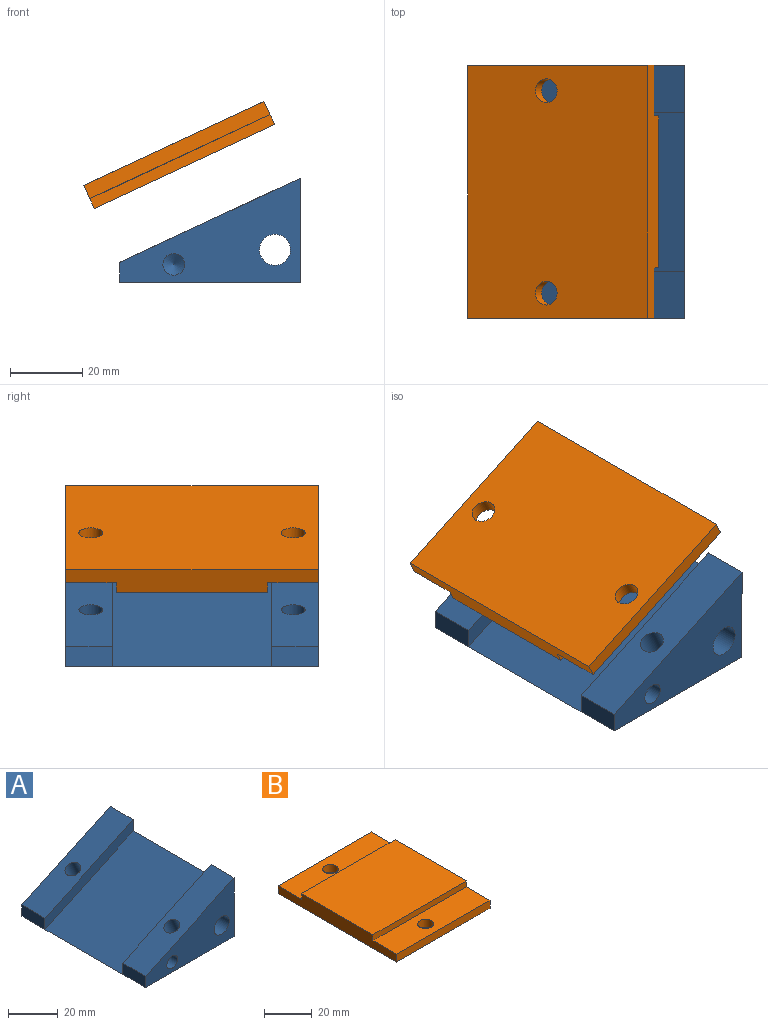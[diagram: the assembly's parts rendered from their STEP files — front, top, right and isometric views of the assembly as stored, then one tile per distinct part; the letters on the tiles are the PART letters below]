
ASSEMBLY  parts=2 mates=1
PART A: 32 faces, bbox 50x70x28.8 mm
  f0: cylinder r=3.3mm len=11.85mm, axis (-0.42,0,0.91), area 207.4mm2, adj f11,f26
  f1: cylinder r=3.3mm len=11.85mm, axis (-0.42,0,0.91), area 207.4mm2, adj f2,f19
  f2: plane 50x23.32mm, normal (-0.42,0,0.91), area 682.9mm2, adj f1,f5,f6,f8,f9
  f3: plane 50x44mm, normal (-0.42,0,0.91), area 2427.4mm2, adj f4,f5,f9,f12
  f4: plane 70x50mm, normal (0,0,-1), area 3285.3mm2, adj f3,f5,f6,f7,f8,f10,f13,f14
  f5: plane 70x28.83mm, normal (1,0,0), area 1775.5mm2, adj f2,f3,f4,f6,f7,f9,f11,f12
  f6: plane 50x28.83mm, normal (0,-1,0), area 772.4mm2, adj f2,f4,f5,f8,f27,f28
  f7: plane 50x28.83mm, normal (0,1,0), area 772.4mm2, adj f4,f5,f10,f11,f27,f30
  f8: plane 13x5.52mm, normal (-1,0,0), area 71.7mm2, adj f2,f4,f6,f9
  f9: plane 50x28.83mm, normal (0,1,0), area 275.8mm2, adj f2,f3,f5,f8
  f10: plane 13x5.52mm, normal (-1,0,0), area 71.7mm2, adj f4,f7,f11,f12
  f11: plane 50x23.31mm, normal (-0.42,0,0.91), area 683mm2, adj f0,f5,f7,f10,f12
  f12: plane 50x28.83mm, normal (0,-1,0), area 275.9mm2, adj f3,f5,f10,f11
  f13: plane 9.23x7.89mm, normal (0,-1,0), area 44.5mm2, adj f4,f14,f18,f19
  f14: plane 9.18x7.06mm, normal (-0.78,-0.5,-0.37), area 57.6mm2, adj f4,f13,f15,f19
  f15: plane 9.18x7.06mm, normal (-0.78,0.5,-0.37), area 57.6mm2, adj f4,f14,f16,f19
  f16: plane 9.23x7.89mm, normal (0,1,0), area 44.5mm2, adj f4,f15,f17,f19
  f17: plane 5.3x5.3mm, normal (0.78,0.5,0.37), area 31.4mm2, adj f4,f16,f18,f19
  f18: plane 5.3x5.3mm, normal (0.78,-0.5,0.37), area 31.4mm2, adj f4,f13,f17,f19
  f19: plane 11.09x10.6mm, normal (0.42,0,-0.91), area 63.1mm2, adj f1,f13,f14,f15,f16,f17,f18
  f20: plane 9.23x7.89mm, normal (0,-1,0), area 44.5mm2, adj f4,f21,f25,f26
  f21: plane 9.18x7.06mm, normal (-0.78,-0.5,-0.37), area 57.6mm2, adj f4,f20,f22,f26
  f22: plane 9.18x7.06mm, normal (-0.78,0.5,-0.37), area 57.6mm2, adj f4,f21,f23,f26
  f23: plane 9.23x7.89mm, normal (0,1,0), area 44.5mm2, adj f4,f22,f24,f26
  f24: plane 5.3x5.3mm, normal (0.78,0.5,0.37), area 31.4mm2, adj f4,f23,f25,f26
  f25: plane 5.3x5.3mm, normal (0.78,-0.5,0.37), area 31.4mm2, adj f4,f20,f24,f26
  f26: plane 11.09x10.6mm, normal (0.42,0,-0.91), area 63.1mm2, adj f0,f20,f21,f22,f23,f24,f25
  f27: cylinder r=4.3mm len=70mm, axis (0,-1,0), area 1891.2mm2, adj f6,f7
  f28: cylinder r=3mm len=10mm, axis (0,-1,0), area 188.5mm2, adj f6,f29
  f29: cone r=0mm half-angle=59deg, axis (0,-1,0), area 33mm2, adj f28
  f30: cylinder r=3mm len=10mm, axis (0,1,0), area 188.5mm2, adj f7,f31
  f31: cone r=0mm half-angle=59deg, axis (0,1,0), area 33mm2, adj f30
PART B: 12 faces, bbox 55x70x7 mm
  f0: plane 55x14mm, normal (0,0,1), area 735.8mm2, adj f1,f2,f3,f6,f9
  f1: plane 70x7mm, normal (-1,0,0), area 406mm2, adj f0,f2,f4,f7,f8,f9,f10,f11
  f2: plane 55x4mm, normal (0,-1,0), area 220mm2, adj f0,f1,f3,f7
  f3: plane 70x7mm, normal (1,0,0), area 406mm2, adj f0,f2,f4,f7,f8,f9,f10,f11
  f4: plane 55x4mm, normal (0,1,0), area 220mm2, adj f1,f3,f7,f8
  f5: cylinder r=3.3mm len=6.6mm, axis (0,0,1), area 82.9mm2, adj f7,f8
  f6: cylinder r=3.3mm len=6.6mm, axis (0,0,1), area 82.9mm2, adj f0,f7
  f7: plane 70x55mm, normal (0,0,-1), area 3781.6mm2, adj f1,f2,f3,f4,f5,f6
  f8: plane 55x14mm, normal (0,0,1), area 735.8mm2, adj f1,f3,f4,f5,f10
  f9: plane 55x3mm, normal (0,-1,0), area 165mm2, adj f0,f1,f3,f11
  f10: plane 55x3mm, normal (0,1,0), area 165mm2, adj f1,f3,f8,f11
  f11: plane 55x42mm, normal (0,0,1), area 2310mm2, adj f1,f3,f9,f10
PLACE A rot(axis=(0.91,0,0.42),0deg) t=(7.12,16.6,22.6)mm
PLACE B rot(axis=(0.98,0,0.22),180deg) t=(48.74,16.6,69.01)mm
MATE cylindrical A.f1 <-> B.f5  axis (-0.42,0,0.91) through (28.88,-11.4,38.26)mm
